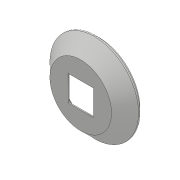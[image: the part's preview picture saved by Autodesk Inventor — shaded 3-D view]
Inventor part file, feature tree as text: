
AUTODESK INVENTOR PART (.ipt)
format: ipt  version: 2017 (Build 210142000, 142)  size: 270,848 bytes
history: native  units: mm
features: sketch x5, fillet x3, extrude x3, revolve x1, shell x1, hole x1, pattern_circular x1, other x1
ambient origin geometry x8: Origin, YZ Plane, XZ Plane, XY Plane, X Axis, Y Axis, Z Axis, Center Point
bodies: Solid1 (feature_tree)
feature tree (16):
  revolve  "Revolution1"  [1 undecoded]
  shell  "Shell1"  Thickness=90.0deg
  fillet  "Fillet1"  Radius=7.0mm
  extrude  "Extrusion1"  TaperAngle=90.0deg  [1 undecoded]
  hole  "Hole1"  [1 undecoded]
  pattern_circular  "Circular Pattern1"  Count=2  [1 undecoded]
  fillet  "Fillet2"  Radius=5.25mm
  fillet  "Fillet3"  Radius=4.5mm
  extrude  "Extrusion2"  Depth=1.75mm
  sketch  "Sketch1"  dims[d1=45.0deg d2=14.0mm d3=90.0deg d4=7.0mm]
  sketch  "Sketch2"  dims[d5=39.375mm d6=90.0deg]
  other  "Srf1"
  sketch  "Sketch3"  dims[d7=1.0mm d8=0.5mm d9=20.0mm d10=0.0mm d11=5.25mm d12=4.5mm]
  sketch  "Sketch4"  dims[d13=0.5mm d14=0.0mm d15=1.75mm]
  sketch  "Sketch5"  dims[d16=1.75mm d17=1.0mm d18=6.0mm d19=4.0mm d20=2.0mm d21=90.0deg d22=8.0mm d23=20.594885mm d24=40.0mm d25=360.0deg d27=1.0mm d28=2.0mm d29=25.0mm d30=25.0mm d31=10.0mm d32=0.0mm]
  extrude  "ExtrusionSrf1"  Depth=10.0mm TaperAngle=360.0deg
note: 4 required parameter values undecoded (feature->parameter linkage not recoverable at this tier; creation-order binding heuristic only, values carry confidence <= 0.55)